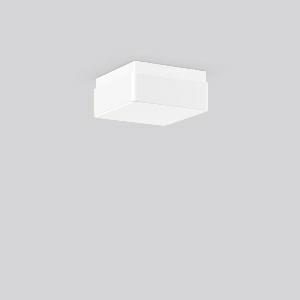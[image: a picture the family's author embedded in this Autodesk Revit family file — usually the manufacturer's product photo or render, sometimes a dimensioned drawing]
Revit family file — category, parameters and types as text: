
# Revit family: quadrat_20128_002_df9f
name_source: partatom
category: Lighting Fixtures
units: mm (PartAtom-declared; Revit-internal decimal feet)

## family parameters
Cut with Voids When Loaded = No
Host = Face
Light Source = No
Part Type = Normal
Room Calculation Point = No
Round Connector Dimension = Use Diameter
Shared = No

## types (1)
- QUADRAT (1 x QA60/clear E27, 915 lm, 57 W, 3000)
    Apparent Load = 57 VA
    CIE Flux Codes = 34 63 85 72 42
    Color Rendering = 90
    Color Temperature = 3000
    Default Elevation = 1800 mm
    Description = Series: QUADRAT
Square surface-mounted luminaire in classic design. Base: plastic. Opal glass: mouth blown, silk finish. Diffuser fastening: spring system. Suitable for Ceiling mounting, Wall (surface). IP 43 ceiling mounting, IP 44 wall mounting. 
Colour: white
Length: 240 mm
Width: 240 mm
Height: 110 mm
Lamp: A60
Number of lamps: 1
Wattage: 75 W
Socket: E27
System power: 60 W
Rated luminous flux: 310 lm
Luminous efficiency: 5 lm/W
Control gear: Converter not necessary
Protection class: II
Type of protection: IP 43
    Height = 110 mm
    Lamp = 1 x QA60/clear E27
    Lamp Light Flux = 915 lm
    Lamp Power = 57 W
    Lamp count = 1
    Length = 240 mm
    Lifetime = 3000 h
    Luminous efficacy = 7 lm/W
    Manufacturer = RZB
    ModVariant = No
    Model = 20128.002
    Mounting Place = Ceiling, Wall
    Mounting Type = Surface mounted
    Number of Poles = 1
    OnlyDefault = Yes
    Power Factor = 1
    Product Name = QUADRAT
    Product group = Surface mounted ceiling and wall luminaires
    ProductGroupID = 305
    Protection Class = Protection class II
    Protection Degree = IP 43
    RLX_Detail_Level = 1
    RLX_Emergency_Light_Flux = 0 lm
    RLX_Emergency_Type = 0
    RLX_Emergency_Type_DB = No
    RlxData = <blob elided: 10069 chars, md5=3e70b765>
    Socket = E27
    Standby Power = 0 W
    System Light Flux = 387 lm
    System Power = 57 W
    Type Comments = Product without accessories
    Type Image = 20128.002.jpg
    URL = http://relux.com
    VarID = ---
    Voltage = 230 V
    Voltage Range = 220-240 V
    Weight = 0.00 kg
    Width = 240 mm

## geometry (parser evidence)
native form markers: Sweep x11
no freeform markers — native parametric forms only
